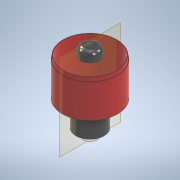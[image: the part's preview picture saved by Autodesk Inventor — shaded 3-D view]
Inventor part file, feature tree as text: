
AUTODESK INVENTOR PART (.ipt)
format: ipt  version: 2020 (Build 240168000, 168)  size: 151,040 bytes
history: native  units: in
note: dims shown in document units (in); Inventor stores cm internally (conversion verified against a paired STEP export)
features: extrude x5, sketch x5, fillet x1, chamfer x1, plane x1
ambient origin geometry x8: Origin, YZ Plane, XZ Plane, XY Plane, X Axis, Y Axis, Z Axis, Center Point
bodies: Solid1 (feature_tree)
feature tree (13):
  extrude  "Extrusion1"  Depth=1.0236in TaperAngle=0.0deg
  extrude  "Extrusion2"  Depth=0.1181in TaperAngle=0.0deg
  extrude  "Extrusion3"  Depth=1.1417in TaperAngle=0.0deg
  extrude  "Extrusion4"  Depth=0.2756in TaperAngle=0.0deg
  fillet  "Fillet1"  Radius=0.1575in
  extrude  "Extrusion5"  Depth=0.9843in TaperAngle=0.0deg
  chamfer  "Chamfer1"  Distance=0.1969in Angle=45.0deg
  plane  "Work Plane1"
  sketch  "Sketch1"  dims[d0=1.6929in d1=1.0236in d2=0.0in]
  sketch  "Sketch2"  dims[d3=1.6535in d4=0.1181in d5=0.0in]
  sketch  "Sketch3"  dims[d6=1.6142in d7=1.1417in d8=0.0in]
  sketch  "Sketch4"  dims[d9=0.5906in d10=0.2756in d11=0.0in d12=0.1575in]
  sketch  "Sketch5"  dims[d13=0.8661in d14=0.9843in d15=0.0in d16=0.1969in d17=0.0787in d18=45.0deg d19=0.0in]
